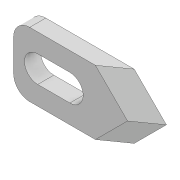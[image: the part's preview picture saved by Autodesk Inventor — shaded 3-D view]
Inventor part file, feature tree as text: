
AUTODESK INVENTOR PART (.ipt)
format: ipt  version: 2022 (Build 260153000, 153)  size: 103,936 bytes
history: native  units: mm
features: extrude x1, chamfer x1, sketch x1
ambient origin geometry x8: Origin, YZ Plane, XZ Plane, XY Plane, X Axis, Y Axis, Z Axis, Center Point
bodies: Body1 (feature_tree)
feature tree (3):
  extrude  "Extrusion2"  Depth=2.0mm
  chamfer  "Chamfer1"  Distance=8.0mm
  sketch  "Sketch1"  dims[d0=3.3mm d1=2.0mm d2=8.0mm d3=4.0mm d4=3.0mm d5=2.0mm d6=45.0deg d7=0.0mm d8=4.0mm d9=10.0mm d10=90.0deg d13=2.0mm d14=0.0mm d15=2.0mm d16=2.0mm d17=45.0deg]
